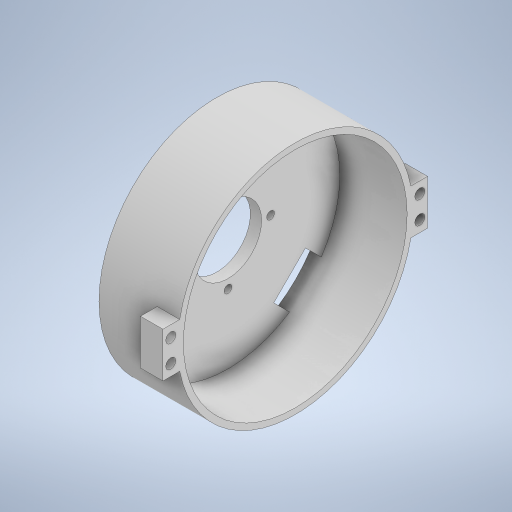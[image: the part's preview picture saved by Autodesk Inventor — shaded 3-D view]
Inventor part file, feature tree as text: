
AUTODESK INVENTOR PART (.ipt)
format: ipt  version: 2023 (Build 270158000, 158)  size: 338,432 bytes
history: native  units: mm
features: extrude x4, sketch x3
ambient origin geometry x8: Origin, YZ Plane, XZ Plane, XY Plane, X Axis, Y Axis, Z Axis, Center Point
bodies: Solid1 (feature_tree)
feature tree (7):
  extrude  "Extrusion1"  Depth=3.5mm
  extrude  "Extrusion2"  Depth=105.0mm
  extrude  "Extrusion3"  Depth=5.0mm TaperAngle=0.0deg
  extrude  "Extrusion4"  Depth=10.0mm
  sketch  "Sketch1"  dims[d0=38.0mm d1=3.5mm]
  sketch  "Sketch2"  dims[d2=40.0mm d4=360.0deg d6=105.0mm]
  sketch  "Sketch3"  dims[d7=80.0mm d8=5.0mm d9=0.0mm d10=105.0mm d11=35.0mm d12=0.0mm d14=10.0mm d15=20.0mm d17=5.0mm d18=4.5mm d19=5.0mm d20=4.5mm d21=20.0mm d23=360.0deg d25=10.0mm d26=0.0mm d27=30.0mm d28=10.0mm d29=45.0deg d30=10.0mm d31=10.0mm d32=0.0mm d33=105.0mm d34=10.0mm d35=0.872665mm d36=0.5mm d37=0.872665mm]
